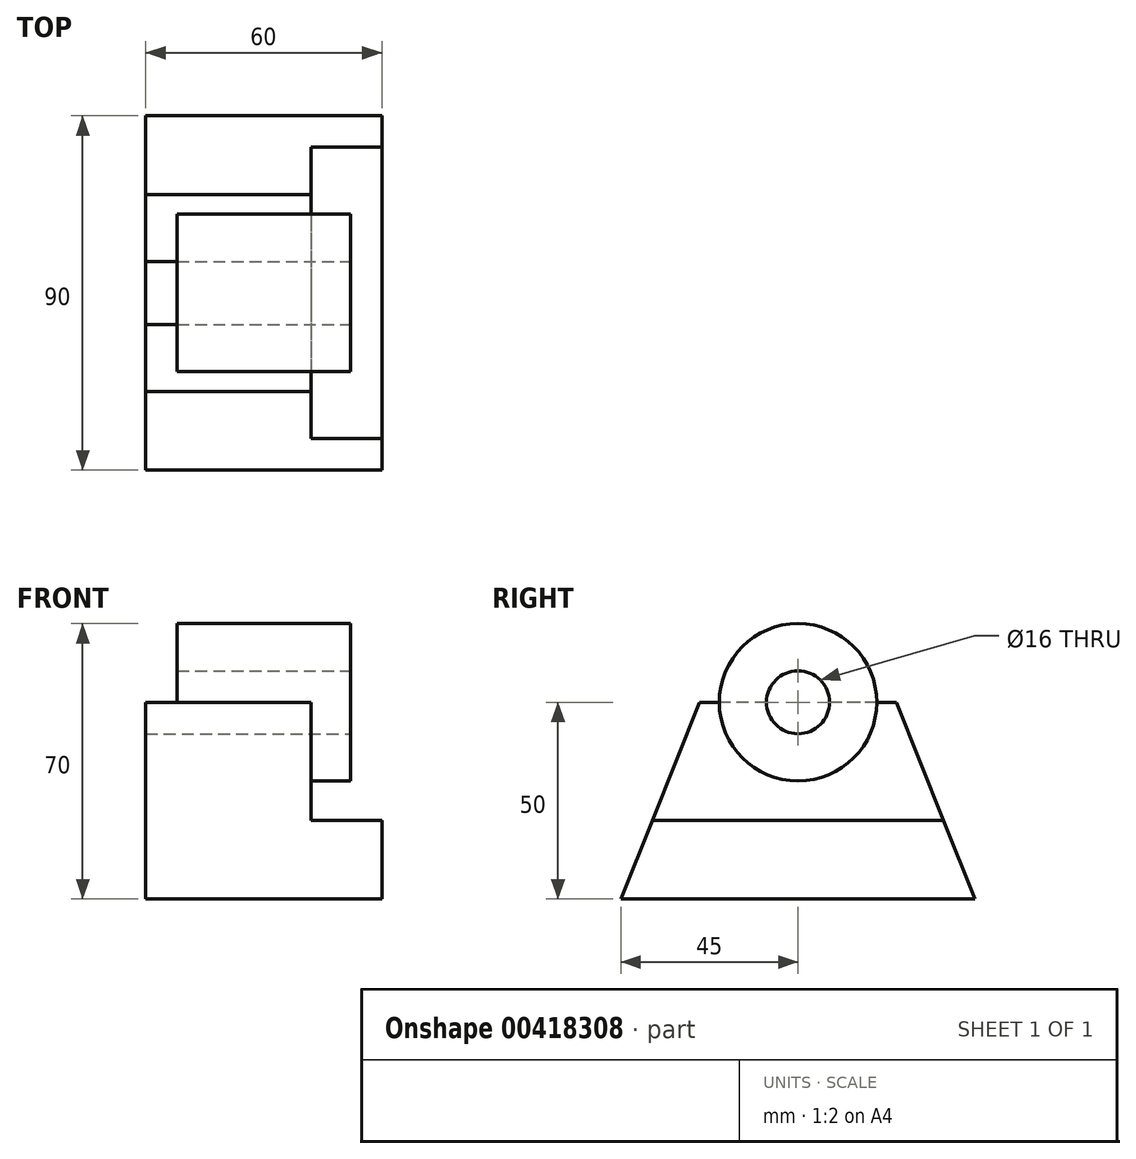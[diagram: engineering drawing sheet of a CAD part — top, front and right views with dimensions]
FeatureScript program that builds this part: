
annotation { "Feature Type Name" : "Feature", "Feature Type Description" : "" }
export const myFeature = defineFeature(function(context is Context, id is Id, definition is map)
    precondition{}
    {
        {
            var Q0;
            Q0=qCreatedBy(makeId("Right.planeOp"),FACE);
            var sketch = newSketch(context, id + "F0", { "sketchPlane" : qUnion([Q0])});
            skLineSegment(sketch, "E0.bottom", {"start": v(45, 25) * mm, "end": v(-45, 25) * mm});
            skLineSegment(sketch, "E0.top", {"start": v(45, -25) * mm, "end": v(-45, -25) * mm});
            skLineSegment(sketch, "E0.left", {"start": v(45, 25) * mm, "end": v(45, -25) * mm});
            skLineSegment(sketch, "E0.right", {"start": v(-45, 25) * mm, "end": v(-45, -25) * mm});
            skPoint(sketch, "E0.middle", {"position": v(0, 0) * mm});
            skSolve(sketch);
        }
        {
            var Q0;
            Q0 = qSketchRegion(id + "F0", true);
            extrude(context, id + "F1", {"entities" : qUnion([Q0]), "endBound" : BoundingType.SYMMETRIC, "depth" : 60 * mm});
        }
        {
            var Q0;
            Q0=makeQuery(id+"F1.opExtrude","SWEPT_EDGE",EDGE,{"disambiguationData":[OSD([sQuery(id+"F0.wireOp",EDGE,"E0.bottom"),sQuery(id+"F0.wireOp",EDGE,"E0.right")])]});
            var Q1;
            Q1=makeQuery(id+"F1.opExtrude","SWEPT_EDGE",EDGE,{"disambiguationData":[OSD([sQuery(id+"F0.wireOp",EDGE,"E0.bottom"),sQuery(id+"F0.wireOp",EDGE,"E0.left")])]});
            chamfer(context, id + "F2", {"entities" : qUnion([Q0, Q1]), "chamferType" : ChamferType.TWO_OFFSETS, "width1" : 50 * mm, "oppositeDirection" : false, "width2" : ((90 - 50) / 2) * mm, "tangentPropagation" : true});
        }
        {
            var Q0;
            Q0=qCreatedBy(makeId("Front.planeOp"),FACE);
            var sketch = newSketch(context, id + "F3", { "sketchPlane" : qUnion([Q0])});
            skLineSegment(sketch, "E1.bottom", {"start": v(12, 25) * mm, "end": v(30, 25) * mm});
            skLineSegment(sketch, "E1.top", {"start": v(12, -5) * mm, "end": v(30, -5) * mm});
            skLineSegment(sketch, "E1.left", {"start": v(12, 25) * mm, "end": v(12, -5) * mm});
            skLineSegment(sketch, "E1.right", {"start": v(30, 25) * mm, "end": v(30, -5) * mm});
            skSolve(sketch);
        }
        {
            var Q0;
            Q0 = qSketchRegion(id + "F3", true);
            extrude(context, id + "F4", {"entities" : qUnion([Q0]), "operationType" : NewBodyOperationType.REMOVE, "endBound" : BoundingType.THROUGH_ALL, "oppositeDirection" : true, "depth" : 25 * mm, "hasSecondDirection" : true, "secondDirectionBound" : SecondDirectionBoundingType.THROUGH_ALL, "secondDirectionOppositeDirection" : false, "secondDirectionDepth" : 25 * mm});
        }
        {
            var Q0;
            Q0=makeQuery(id+"F4.boolean.opBoolean","COPY",FACE,{"derivedFrom":makeQuery(id+"F4.opExtrude","SWEPT_FACE",FACE,{"disambiguationData":[OSD([sQuery(id+"F3.wireOp",EDGE,"E1.left")])]})});
            var sketch = newSketch(context, id + "F5", { "sketchPlane" : qUnion([Q0])});
            skCircle(sketch, "E2", {"center": v(0, 25) * mm, "radius": 20 * mm});
            skSolve(sketch);
        }
        {
            var Q0;
            Q0 = qSketchRegion(id + "F5", true);
            extrude(context, id + "F6", {"entities" : qUnion([Q0]), "operationType" : NewBodyOperationType.ADD, "depth" : 10 * mm, "hasSecondDirection" : true, "secondDirectionOppositeDirection" : true, "secondDirectionDepth" : 34 * mm});
        }
        {
            var Q0;
            Q0=makeQuery(id+"F6.opExtrude","CAP_FACE",FACE,{"disambiguationData":[OSD([sQuery(id+"F5.wireOp",EDGE,"E2")])],"isStart":false});
            var sketch = newSketch(context, id + "F7", { "sketchPlane" : qUnion([Q0])});
            skCircle(sketch, "E3", {"center": v(0, 25) * mm, "radius": 8 * mm});
            skSolve(sketch);
        }
        {
            var Q0;
            Q0 = qSketchRegion(id + "F7", true);
            extrude(context, id + "F8", {"entities" : qUnion([Q0]), "operationType" : NewBodyOperationType.REMOVE, "endBound" : BoundingType.THROUGH_ALL, "oppositeDirection" : true, "depth" : 25 * mm});
        }
    });
